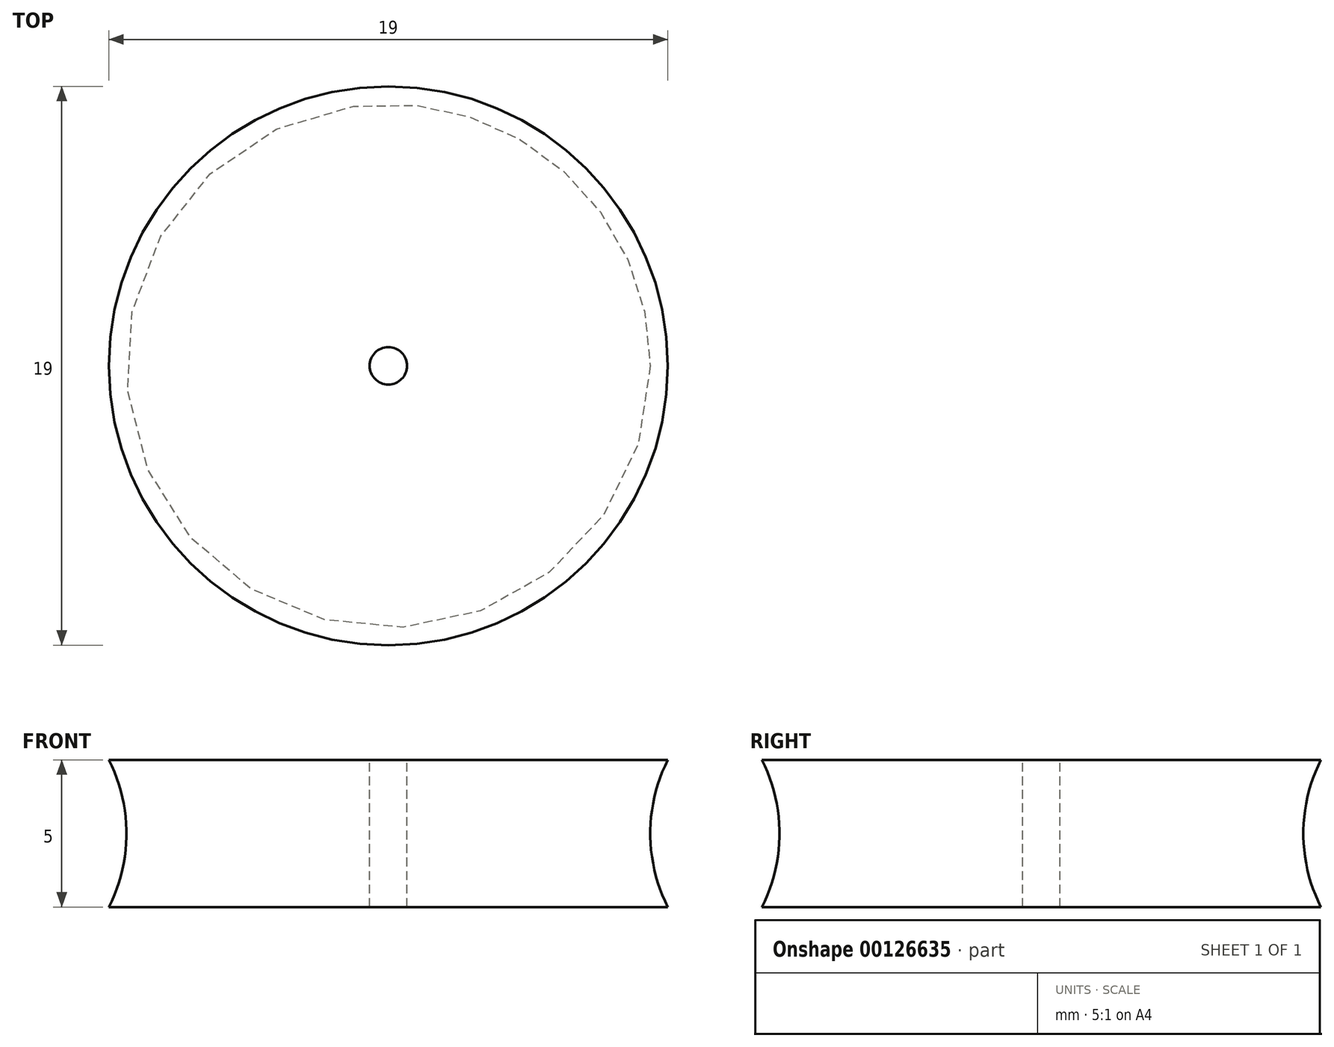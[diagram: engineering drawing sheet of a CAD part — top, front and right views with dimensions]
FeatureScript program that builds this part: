
annotation { "Feature Type Name" : "Feature", "Feature Type Description" : "" }
export const myFeature = defineFeature(function(context is Context, id is Id, definition is map)
    precondition{}
    {
        {
            var Q0;
            Q0=qCreatedBy(makeId("Front.planeOp"),FACE);
            var sketch = newSketch(context, id + "F0", { "sketchPlane" : qUnion([Q0])});
            skLineSegment(sketch, "E0", {"start": v(-0.64, 2.5) * mm, "end": v(-0.63, -2.5) * mm});
            skLineSegment(sketch, "E1", {"start": v(-0.63, -2.5) * mm, "end": v(-9.5, -2.5) * mm});
            skLineSegment(sketch, "E2", {"start": v(-0.63, 2.5) * mm, "end": v(-9.5, 2.5) * mm});
            skArc(sketch, "E3", {"start": v(-9.5, -2.5) * mm, "mid": v(-8.9, 0) * mm, "end": v(-9.5, 2.5) * mm});
            skLineSegment(sketch, "E4", {"start": v(0, 5.55) * mm, "end": v(0, -5.78) * mm});
            skSolve(sketch);
        }
        {
            var Q0;
            Q0=makeQuery(id+"F0.imprint","IMPRINT",FACE,{"disambiguationData":[TD([[makeQuery(id+"F0.imprint","IMPRINT",EDGE,{"derivedFrom":sQuery(id+"F0.wireOp",EDGE,"E0")}),-1.0]])]});
            var Q1;
            Q1=sQuery(id+"F0.wireOp",EDGE,"E4");
            revolve(context, id + "F1", {"entities" : qUnion([Q0]), "axis" : qUnion([Q1]), "revolveType" : RevolveType.FULL});
        }
    });
